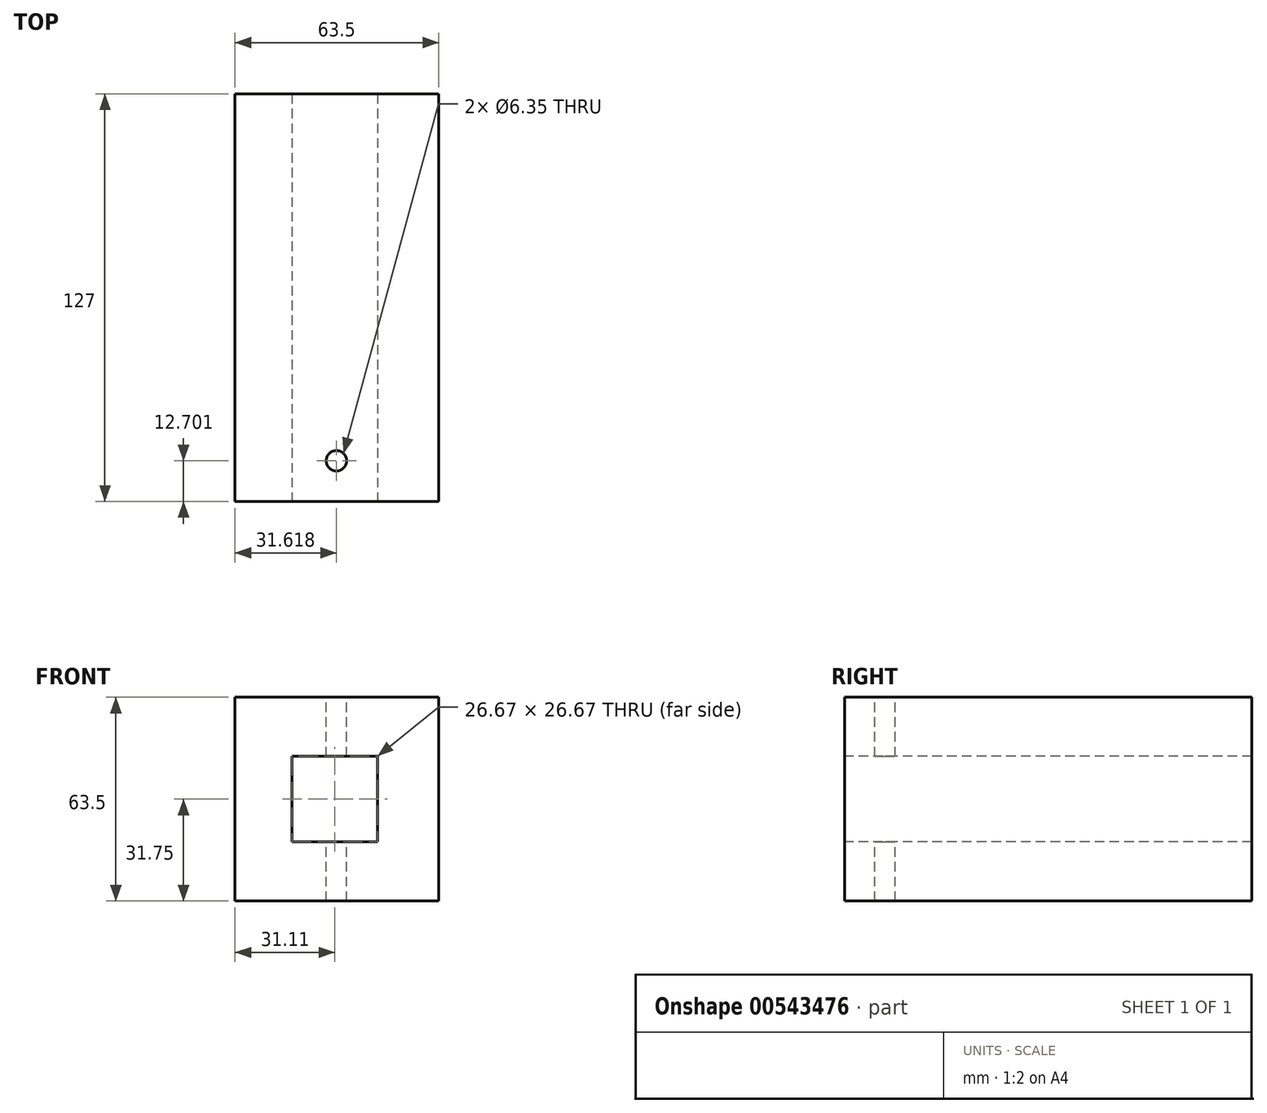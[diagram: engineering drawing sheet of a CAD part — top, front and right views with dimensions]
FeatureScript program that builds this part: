
annotation { "Feature Type Name" : "Feature", "Feature Type Description" : "" }
export const myFeature = defineFeature(function(context is Context, id is Id, definition is map)
    precondition{}
    {
        {
            var Q0;
            Q0=qCreatedBy(makeId("Top.planeOp"),FACE);
            var sketch = newSketch(context, id + "F0", { "sketchPlane" : qUnion([Q0])});
            skLineSegment(sketch, "E0.bottom", {"start": v(-30.45, 93.7) * mm, "end": v(33.05, 93.7) * mm});
            skLineSegment(sketch, "E0.top", {"start": v(-30.45, -33.3) * mm, "end": v(33.05, -33.3) * mm});
            skLineSegment(sketch, "E0.left", {"start": v(-30.45, 93.7) * mm, "end": v(-30.45, -33.3) * mm});
            skLineSegment(sketch, "E0.right", {"start": v(33.05, 93.7) * mm, "end": v(33.05, -33.3) * mm});
            skSolve(sketch);
        }
        {
            var Q0;
            Q0=makeQuery(id+"F0.imprint","IMPRINT",FACE,{"disambiguationData":[TD([[makeQuery(id+"F0.imprint","IMPRINT",EDGE,{"derivedFrom":sQuery(id+"F0.wireOp",EDGE,"E0.bottom")}),-1.0]])]});
            extrude(context, id + "F1", {"entities" : qUnion([Q0]), "depth" : 63.5 * mm, "offsetDistance" : 25.4 * mm});
        }
        {
            var Q0;
            Q0=makeQuery(id+"F1.opExtrude","SWEPT_FACE",FACE,{"disambiguationData":[OSD([sQuery(id+"F0.wireOp",EDGE,"E0.top")])]});
            var sketch = newSketch(context, id + "F2", { "sketchPlane" : qUnion([Q0])});
            skLineSegment(sketch, "E1.bottom", {"start": v(14, 45.09) * mm, "end": v(-12.67, 45.09) * mm});
            skLineSegment(sketch, "E1.top", {"start": v(14, 18.41) * mm, "end": v(-12.67, 18.41) * mm});
            skLineSegment(sketch, "E1.left", {"start": v(14, 45.09) * mm, "end": v(14, 18.41) * mm});
            skLineSegment(sketch, "E1.right", {"start": v(-12.67, 45.09) * mm, "end": v(-12.67, 18.41) * mm});
            skSolve(sketch);
        }
        {
            var Q0;
            Q0=makeQuery(id+"F2.imprint","IMPRINT",FACE,{"disambiguationData":[TD([[makeQuery(id+"F2.imprint","IMPRINT",EDGE,{"derivedFrom":sQuery(id+"F2.wireOp",EDGE,"E1.bottom")}),1.0]])]});
            extrude(context, id + "F3", {"entities" : qUnion([Q0]), "operationType" : NewBodyOperationType.REMOVE, "endBound" : BoundingType.THROUGH_ALL, "oppositeDirection" : true, "depth" : 27.94 * mm, "offsetDistance" : 25.4 * mm});
        }
        {
            var Q0;
            Q0=makeQuery(id+"F3.boolean.opBoolean","COPY",FACE,{"derivedFrom":makeQuery(id+"F3.opExtrude","SWEPT_FACE",FACE,{"disambiguationData":[OSD([sQuery(id+"F2.wireOp",EDGE,"E1.bottom")])]})});
            var sketch = newSketch(context, id + "F4", { "sketchPlane" : qUnion([Q0])});
            skCircle(sketch, "E2", {"center": v(1.17, 20.6) * mm, "radius": 3.18 * mm});
            skLineSegment(sketch, "E3", {"start": v(-12.67, -30.2) * mm, "end": v(14, -30.2) * mm, "construction": true});
            skPoint(sketch, "E3.endSnap0", {"position": v(14, -30.2) * mm});
            skSolve(sketch);
        }
        {
            var Q0;
            Q0=makeQuery(id+"F4.imprint","IMPRINT",FACE,{"disambiguationData":[TD([[makeQuery(id+"F4.imprint","IMPRINT",EDGE,{"derivedFrom":sQuery(id+"F4.wireOp",EDGE,"E2")}),1.0]])]});
            extrude(context, id + "F5", {"entities" : qUnion([Q0]), "operationType" : NewBodyOperationType.REMOVE, "endBound" : BoundingType.THROUGH_ALL, "depth" : 25.4 * mm, "offsetDistance" : 25.4 * mm, "hasSecondDirection" : true, "secondDirectionOppositeDirection" : true, "secondDirectionDepth" : 25.4 * mm});
        }
    });
